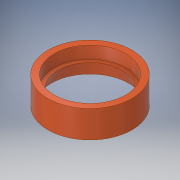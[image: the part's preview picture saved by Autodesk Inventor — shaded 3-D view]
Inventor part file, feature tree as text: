
AUTODESK INVENTOR PART (.ipt)
format: ipt  version: 2017 (Build 210142000, 142)  size: 143,872 bytes
history: native  units: in
note: dims shown in document units (in); Inventor stores cm internally (conversion verified against a paired STEP export)
features: revolve x1, sketch x1
ambient origin geometry x8: Origin, YZ Plane, XZ Plane, XY Plane, X Axis, Y Axis, Z Axis, Center Point
bodies: Body1 (feature_tree)
feature tree (2):
  revolve  "Revolution3"  [1 undecoded]
  sketch  "Sketch1"  dims[d0=0.25in d1=0.1718in d2=15.0deg d4=0.25in d5=1.5in d6=1.25in d7=0.25in d11=0.25in d13=0.5in d15=0.25in d16=0.25in d18=0.125in d19=0.5in d20=0.125in d21=0.25in d22=0.125in d23=0.125in d24=0.25in d25=0.5in d26=2.292in d27=0.5in d29=0.5in d31=90.0deg]
note: 1 required parameter value undecoded (feature->parameter linkage not recoverable at this tier; creation-order binding heuristic only, values carry confidence <= 0.55)
